# Revit family: DCS_3D_Revit_18_WD1-30-SSOD_Warming_Drawer_9000xxxxxxA
name_source: partatom
category: Specialty Equipment
revit_build: Autodesk Revit 2018 (Build: 20170223_1515(x64)
units: mm (PartAtom-declared; Revit-internal decimal feet)

## family parameters
Always vertical = Yes
Cut with Voids When Loaded = Yes
OmniClass Number = 23.40.40.00
OmniClass Title = Food Service Equipment and Furnishings
Part Type = Normal
Room Calculation Point = No
Round Connector Dimension = Use Diameter
Shared = No
Work Plane-Based = No

## types (1)
- DCS_3D_Revit_18_WD1-30-SSOD_Warming_Drawer_9000xxxxxxA
    Cavity - Depth = 613 mm  [stored 2.01115 ft]
    Cavity - Height = 372 mm  [stored 1.22047 ft]
    Cavity - Width = 720 mm  [stored 2.3622 ft]
    Chassis - Depth = 590 mm  [stored 1.9357 ft]
    Chassis - Height = 367 mm  [stored 1.20407 ft]
    Chassis - Width = 715 mm  [stored 2.3458 ft]
    Connector Description - Electrical = 110-120 V, 60 Hz, 15 A dedicated circuit
    Manufacturer = Fisher & Paykel Appliances
    Material - Body = DCS - Grey
    Material - Door Front = DCS - Stainless Steel
    Material - Glass = DCS - Bezel Red
    Material - Handle = DCS - Aluminium
    Product - Depth = 640 mm  [stored 2.09974 ft]
    Product - Height = 406 mm  [stored 1.33202 ft]
    Product - Width = 762 mm  [stored 2.5 ft]
    URL = www.dcsappliances.com
    Visibility - Clearance Required = Yes

note: [stored X ft] marks values corroborated as IEEE doubles in the binary element streams (Revit-internal decimal feet)

## geometry (parser evidence)
native form markers: Sweep x3
no freeform markers — native parametric forms only
